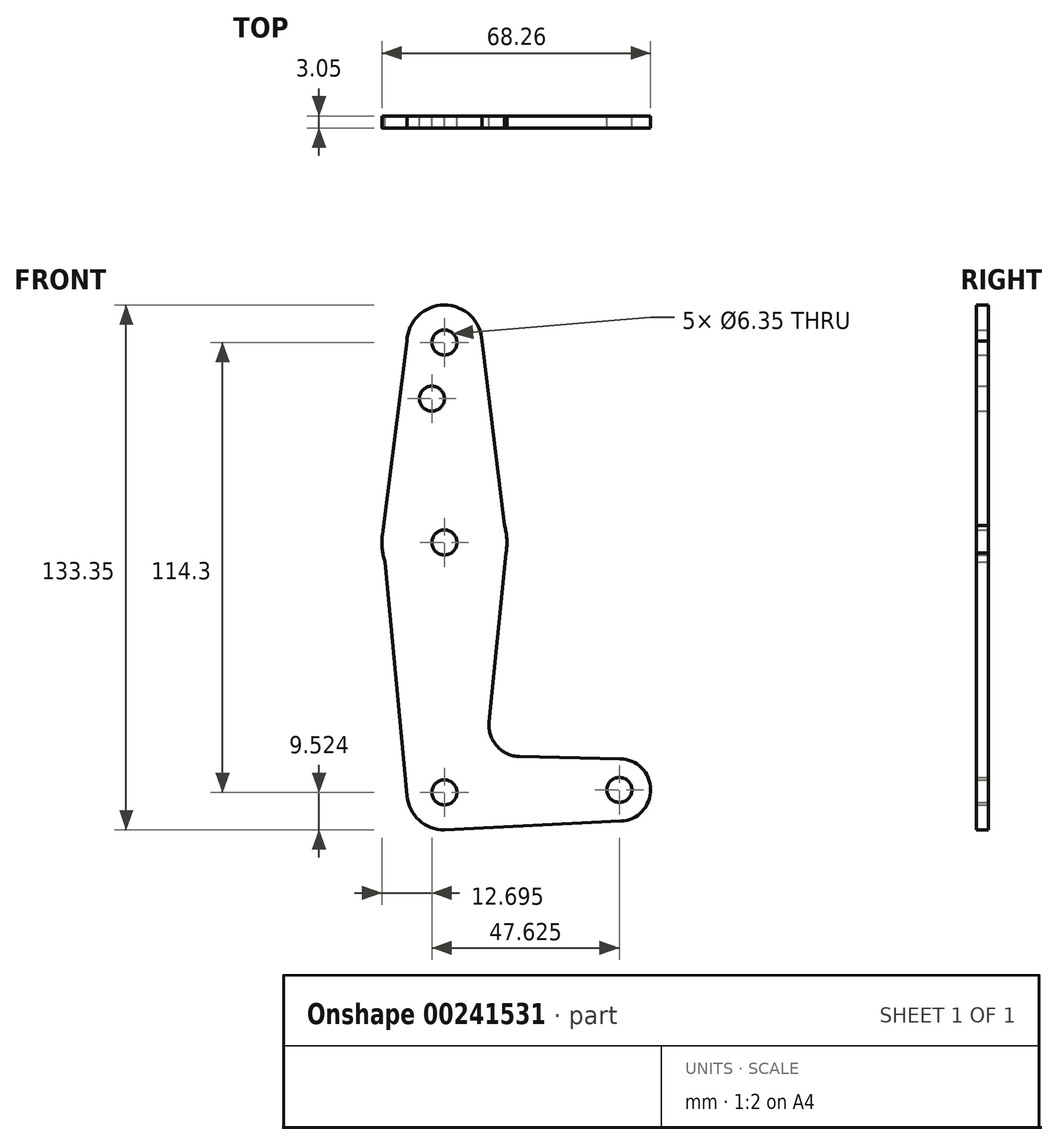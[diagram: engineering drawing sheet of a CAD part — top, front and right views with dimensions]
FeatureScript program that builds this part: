
annotation { "Feature Type Name" : "Feature", "Feature Type Description" : "" }
export const myFeature = defineFeature(function(context is Context, id is Id, definition is map)
    precondition{}
    {
        {
            var Q0;
            Q0=qCreatedBy(makeId("Front.planeOp"),FACE);
            var sketch = newSketch(context, id + "F0", { "sketchPlane" : qUnion([Q0])});
            skCircle(sketch, "E0", {"center": v(0, 58) * mm, "radius": 9.53 * mm});
            skCircle(sketch, "E1", {"center": v(0, 7.2) * mm, "radius": 15.88 * mm});
            skCircle(sketch, "E2", {"center": v(0, -56.3) * mm, "radius": 9.53 * mm});
            skCircle(sketch, "E3", {"center": v(44.45, -55.68) * mm, "radius": 7.94 * mm});
            skCircle(sketch, "E4", {"center": v(0, 58) * mm, "radius": 3.18 * mm});
            skCircle(sketch, "E5", {"center": v(0, 7.2) * mm, "radius": 3.18 * mm});
            skCircle(sketch, "E6", {"center": v(0, -56.3) * mm, "radius": 3.18 * mm});
            skCircle(sketch, "E7", {"center": v(44.45, -55.68) * mm, "radius": 3.18 * mm});
            skCircle(sketch, "E8", {"center": v(-3.18, 43.72) * mm, "radius": 3.18 * mm});
            skLineSegment(sketch, "E9", {"start": v(-9.52, 58.32) * mm, "end": v(-15.75, 9.2) * mm});
            skLineSegment(sketch, "E10", {"start": v(-15.75, 9.2) * mm, "end": v(-9.48, -57.2) * mm});
            skLineSegment(sketch, "E11", {"start": v(9.52, 58.33) * mm, "end": v(15.87, 6.67) * mm});
            skLineSegment(sketch, "E12", {"start": v(15.87, 6.67) * mm, "end": v(11.36, -38.45) * mm});
            skLineSegment(sketch, "E13", {"start": v(19.1, -47.2) * mm, "end": v(44.62, -47.74) * mm});
            skLineSegment(sketch, "E14", {"start": v(0, -65.83) * mm, "end": v(44.84, -63.6) * mm});
            skPoint(sketch, "E15.newPointB", {"position": v(0, -46.78) * mm});
            skArc(sketch, "E15.filletArc", {"start": v(11.36, -38.45) * mm, "mid": v(13.32, -44.52) * mm, "end": v(19.1, -47.2) * mm});
            skSolve(sketch);
        }
        {
            var Q0;
            {var subQ0=sQuery(id+"F0.wireOp",EDGE,"E10");var subQ1=sQuery(id+"F0.wireOp",EDGE,"E1");var subQ3=makeQuery(id+"F0.imprint","INTERSECT",VERTEX,{"derivedFrom":[subQ1,subQ0]});Q0=makeQuery(id+"F0.imprint","IMPRINT",FACE,{"disambiguationData":[TD([[makeQuery(id+"F0.imprint","IMPRINT",EDGE,{"disambiguationData":[TD([[subQ3,1.0]])],"derivedFrom":subQ1}),1.0]])]});}
            var Q1;
            {var subQ0=sQuery(id+"F0.wireOp",EDGE,"E12");var subQ1=sQuery(id+"F0.wireOp",EDGE,"E1");var subQ3=makeQuery(id+"F0.imprint","INTERSECT",VERTEX,{"derivedFrom":[subQ1,subQ0]});Q1=makeQuery(id+"F0.imprint","IMPRINT",FACE,{"disambiguationData":[TD([[makeQuery(id+"F0.imprint","IMPRINT",EDGE,{"disambiguationData":[TD([[subQ3,-1.0]])],"derivedFrom":subQ1}),1.0]])]});}
            var Q2;
            {var subQ0=sQuery(id+"F0.wireOp",EDGE,"E11");var subQ1=sQuery(id+"F0.wireOp",EDGE,"E1");var subQ3=makeQuery(id+"F0.imprint","INTERSECT",VERTEX,{"derivedFrom":[subQ1,subQ0]});Q2=makeQuery(id+"F0.imprint","IMPRINT",FACE,{"disambiguationData":[TD([[makeQuery(id+"F0.imprint","IMPRINT",EDGE,{"disambiguationData":[TD([[subQ3,1.0]])],"derivedFrom":subQ1}),1.0]])]});}
            var Q3;
            {var subQ0=sQuery(id+"F0.wireOp",EDGE,"E14");var subQ1=sQuery(id+"F0.wireOp",EDGE,"E2");var subQ2=makeQuery(id+"F0.imprint","INTERSECT",VERTEX,{"disambiguationData":[OD(0.0)],"derivedFrom":[subQ1,subQ0]});Q3=makeQuery(id+"F0.imprint","IMPRINT",FACE,{"disambiguationData":[TD([[makeQuery(id+"F0.imprint","IMPRINT",EDGE,{"disambiguationData":[TD([[subQ2,-1.0]])],"derivedFrom":subQ1}),1.0]])]});}
            var Q4;
            Q4=makeQuery(id+"F0.imprint","IMPRINT",FACE,{"disambiguationData":[TD([[makeQuery(id+"F0.imprint","IMPRINT",EDGE,{"derivedFrom":sQuery(id+"F0.wireOp",EDGE,"E4")}),-1.0]])]});
            var Q5;
            Q5=makeQuery(id+"F0.imprint","IMPRINT",FACE,{"disambiguationData":[TD([[makeQuery(id+"F0.imprint","IMPRINT",EDGE,{"derivedFrom":sQuery(id+"F0.wireOp",EDGE,"E7")}),-1.0]])]});
            var Q6;
            {var subQ0=sQuery(id+"F0.wireOp",EDGE,"E13");Q6=makeQuery(id+"F0.imprint","IMPRINT",FACE,{"disambiguationData":[TD([[makeQuery(id+"F0.imprint","IMPRINT",EDGE,{"derivedFrom":subQ0}),-1.0]])]});}
            var Q7;
            Q7=makeQuery(id+"F0.imprint","IMPRINT",FACE,{"disambiguationData":[TD([[makeQuery(id+"F0.imprint","IMPRINT",EDGE,{"derivedFrom":sQuery(id+"F0.wireOp",EDGE,"E6")}),-1.0]])]});
            var Q8;
            Q8=makeQuery(id+"F0.imprint","IMPRINT",FACE,{"disambiguationData":[TD([[makeQuery(id+"F0.imprint","IMPRINT",EDGE,{"derivedFrom":sQuery(id+"F0.wireOp",EDGE,"E5")}),-1.0]])]});
            var Q9;
            Q9=makeQuery(id+"F0.imprint","IMPRINT",FACE,{"disambiguationData":[TD([[makeQuery(id+"F0.imprint","IMPRINT",EDGE,{"derivedFrom":sQuery(id+"F0.wireOp",EDGE,"E8")}),-1.0]])]});
            extrude(context, id + "F1", {"entities" : qUnion([Q0, Q1, Q2, Q3, Q4, Q5, Q6, Q7, Q8, Q9]), "depth" : 3.05 * mm});
        }
    });
